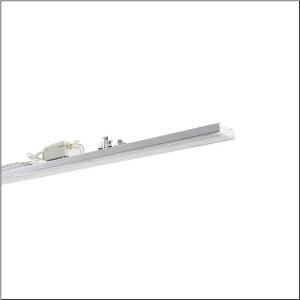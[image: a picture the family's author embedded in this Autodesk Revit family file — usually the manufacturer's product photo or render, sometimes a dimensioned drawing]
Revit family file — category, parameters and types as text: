
# Revit family: licross_r__11_recessed_ho_51tl18de465m_b9d1
name_source: partatom
category: Lighting Fixtures
units: mm (PartAtom-declared; Revit-internal decimal feet)

## family parameters
Cut with Voids When Loaded = No
Host = Face
Light Source = No
Part Type = Normal
Room Calculation Point = No
Round Connector Dimension = Use Diameter
Shared = No

## types (1)
- --- (1 x LED, 6940 lm, 40.2 W, 4000K)
    Apparent Load = 40 VA
    CIE Flux Codes = 78 94 99 100 100
    Color Rendering = 80
    Color Temperature = 4000K
    Default Elevation = 1800 mm
    Description = Licross® 11 Recessed HO, luminaire insert, of sheet steel, coil coated, white, length: 750mm, width: 66mm, height: 67mm, LED rated luminous flux: 6.940lm, light colour: 840, control gear: DALI 2, with plug, 5-pole, with phase selection, mains connection: 220..240V, AC, 50/60Hz, rated input power: 40W, halogen-free wiring, primary light control with lens, of plastic, primary optical cover: cover, of PMMA, light emission: direct distribution, primary light characteristic: symmetric, protection rating (complete): IP40, insulation class (complete): insulation class I (protective earthing), certification: CE, ENEC, VDE, UKCA, protection symbol: D if used in an environment without relevant dust loads with corresponding accessories, impact resistance: IK06, permissible ambient temperature for indoor applications: -25..+35°C, corresponds to IFS (International Featured Standards) requirements for safety and quality in the food industry, reducing of maximum allowable ambient temperature of 5°C with ceiling mounting, LABS conformity tested according to VDMA 24364:2018-05, packaging unit: 1 piece
    Height = 58 mm
    Lamp = 1 x LED
    Lamp Light Flux = 6940 lm
    Lamp Power = 40.2 W
    Lamp count = 1
    Length = 750 mm
    Luminous efficacy = 173 lm/W
    Manufacturer = Siteco
    ModVariant = No
    Model = 51TL18DE465M
    Mounting Place = Ceiling
    Mounting Type = Pendant
    Number of Poles = 1
    OnlyDefault = Yes
    Power Factor = 1
    Product Name = Licross® 11 Recessed HO
    Product group = luminaire insert
    ProductGroupID = 901
    Protection Class = Protection class I
    Protection Degree = IP 40
    RLX_Detail_Level = 1
    RLX_Emergency_Light_Flux = 0 lm
    RLX_Emergency_Type = 0
    RLX_Emergency_Type_DB = No
    RlxData = <blob elided: 29385 chars, md5=c9a976a7>
    Socket = socket
    Standby Power = 0 W
    System Light Flux = 6940 lm
    System Power = 40 W
    Type Comments = factory setting: luminous flux: 100 % | dim-lin: 254 | 522 mA
    Type Image = l_1296930.jpg
    URL = http://relux.com
    VarID = @adj_068085
    Voltage = 0 V
    Weight = 0.00 kg
    Width = 66 mm

## geometry (parser evidence)
native form markers: Blend x4, Sweep x12
no freeform markers — native parametric forms only
